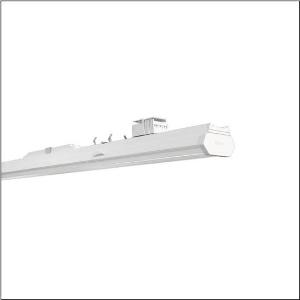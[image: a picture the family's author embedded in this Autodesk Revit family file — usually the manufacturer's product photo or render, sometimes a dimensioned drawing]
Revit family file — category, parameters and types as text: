
# Revit family: licross_r__21_protected_ho_52td1bdn4d5m_ff94
name_source: partatom
category: Lighting Fixtures
units: mm (PartAtom-declared; Revit-internal decimal feet)

## family parameters
Cut with Voids When Loaded = No
Host = Face
Light Source = No
Part Type = Normal
Room Calculation Point = No
Round Connector Dimension = Use Diameter
Shared = No

## types (1)
- --- (1 x LED, 13950 lm, 84.9 W, 4000K)
    Apparent Load = 85 VA
    CIE Flux Codes = 54 82 95 97 100
    Color Rendering = 80
    Color Temperature = 4000K
    Default Elevation = 1800 mm
    Description = Licross® 21 Protected HO, luminaire insert, of sheet steel, galvanised, coil coated, white, length: 1.500mm, width: 90mm, height: 103mm, LED rated luminous flux: 13.950lm, light colour: 840, control gear: DALI 2, with plug, 5-pole, with phase selection, mains connection: 220..240V, AC, 50/60Hz, rated input power: 85W, halogen-free wiring, primary optical cover: cover, of PMMA, light emission: direct distribution, primary light characteristic: symmetric, protection rating (complete): IP54, insulation class (complete): insulation class I (protective earthing), certification: CE, ENEC, VDE, UKCA, protection symbol: D if used in an environment with non-conductive dust loads with corresponding accessories, impact resistance: IK06, permissible ambient temperature for indoor applications: -25..+35°C, corresponds to IFS (International Featured Standards) requirements for safety and quality in the food industry, reducing of maximum allowable ambient temperature of 5°C with ceiling mounting, LABS conformity tested according to VDMA 24364:2018-05, packaging unit: 1 piece
    Height = 92 mm
    Lamp = 1 x LED
    Lamp Light Flux = 13950 lm
    Lamp Power = 84.9 W
    Lamp count = 1
    Length = 1500 mm
    Luminous efficacy = 164 lm/W
    Manufacturer = Siteco
    ModVariant = No
    Model = 52TD1BDN4D5M
    Mounting Place = Ceiling
    Mounting Type = Pendant
    Number of Poles = 1
    OnlyDefault = Yes
    Power Factor = 1
    Product Name = Licross® 21 Protected HO
    Product group = luminaire insert
    ProductGroupID = 901
    Protection Class = Protection class I
    Protection Degree = IP 54
    RLX_Detail_Level = 1
    RLX_Emergency_Light_Flux = 0 lm
    RLX_Emergency_Type = 0
    RLX_Emergency_Type_DB = No
    RlxData = <blob elided: 24405 chars, md5=932e4a94>
    Socket = socket
    Standby Power = 0 W
    System Light Flux = 13950 lm
    System Power = 85 W
    Type Comments = factory setting: luminous flux: 100 % | dim-lin: 254 | 484 mA
    Type Image = l_1256148.jpg
    URL = http://relux.com
    VarID = @adj_078789
    Voltage = 0 V
    Weight = 0.00 kg
    Width = 88 mm

## geometry (parser evidence)
native form markers: Blend x4, Sweep x10
no freeform markers — native parametric forms only
